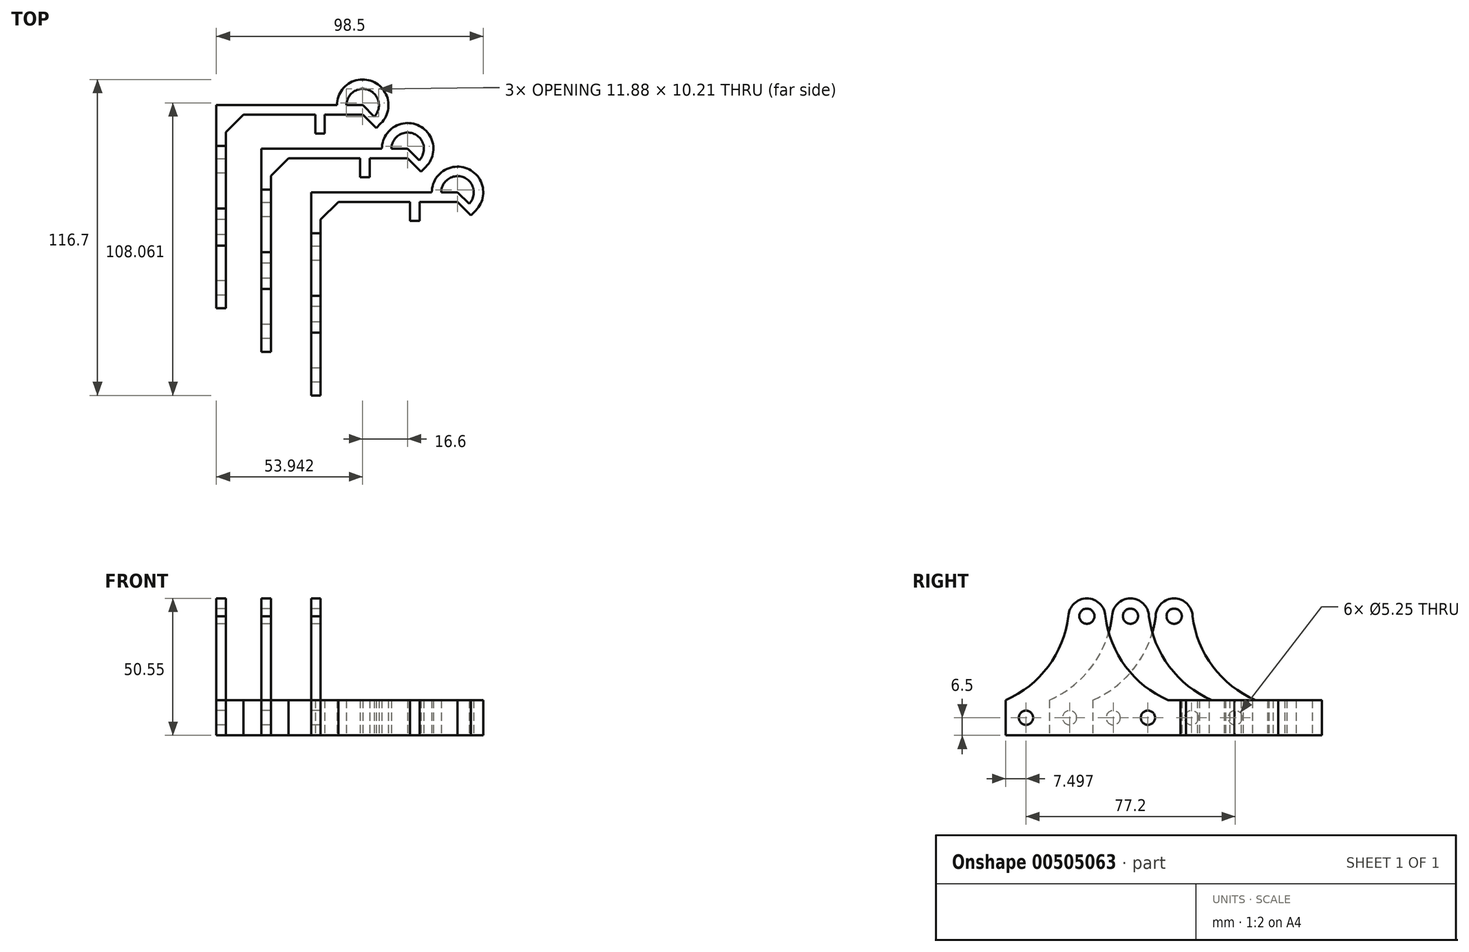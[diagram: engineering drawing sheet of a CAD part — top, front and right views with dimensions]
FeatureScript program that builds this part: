
annotation { "Feature Type Name" : "Feature", "Feature Type Description" : "" }
export const myFeature = defineFeature(function(context is Context, id is Id, definition is map)
    precondition{}
    {
        {
            var Q0;
            Q0=qCreatedBy(makeId("Top.planeOp"),FACE);
            var sketch = newSketch(context, id + "F0", { "sketchPlane" : qUnion([Q0])});
            skLineSegment(sketch, "E0", {"start": v(-36.5, -18.83) * mm, "end": v(-36.5, 56.17) * mm});
            skLineSegment(sketch, "E1", {"start": v(-36.5, 56.17) * mm, "end": v(8, 56.17) * mm});
            skLineSegment(sketch, "E2", {"start": v(17.5, 56.17) * mm, "end": v(21.74, 51.92) * mm});
            skArc(sketch, "E3", {"start": v(21.74, 51.92) * mm, "mid": v(19.8, 61.71) * mm, "end": v(11.5, 56.17) * mm});
            skArc(sketch, "E4", {"start": v(24.22, 49.45) * mm, "mid": v(21.14, 64.94) * mm, "end": v(8, 56.17) * mm});
            skLineSegment(sketch, "E5", {"start": v(-36.5, -18.83) * mm, "end": v(-33, -18.83) * mm});
            skLineSegment(sketch, "E6", {"start": v(-33, -18.83) * mm, "end": v(-33, 46.17) * mm});
            skLineSegment(sketch, "E7", {"start": v(-33, 46.17) * mm, "end": v(-26.5, 52.67) * mm});
            skLineSegment(sketch, "E8", {"start": v(-26.5, 52.67) * mm, "end": v(0, 52.67) * mm});
            skLineSegment(sketch, "E9", {"start": v(24.22, 49.45) * mm, "end": v(22.47, 47.7) * mm});
            skLineSegment(sketch, "E10", {"start": v(17.5, 52.67) * mm, "end": v(22.47, 47.7) * mm});
            skLineSegment(sketch, "E11.trimOffspring", {"start": v(11.5, 56.17) * mm, "end": v(17.5, 56.17) * mm});
            skPoint(sketch, "E12", {"position": v(-36.5, -11.83) * mm});
            skPoint(sketch, "E13", {"position": v(-36.5, 33.17) * mm});
            skPoint(sketch, "E14", {"position": v(0, 52.67) * mm});
            skLineSegment(sketch, "E15", {"start": v(0, 52.67) * mm, "end": v(0, 45.67) * mm});
            skLineSegment(sketch, "E16", {"start": v(0, 45.67) * mm, "end": v(3.5, 45.67) * mm});
            skLineSegment(sketch, "E17", {"start": v(3.5, 45.67) * mm, "end": v(3.5, 52.67) * mm});
            skLineSegment(sketch, "E18.trimOffspring", {"start": v(3.5, 52.67) * mm, "end": v(17.5, 52.67) * mm});
            skSolve(sketch);
        }
        {
            var Q0;
            Q0=makeQuery(id+"F0.imprint","IMPRINT",FACE,{"disambiguationData":[TD([[makeQuery(id+"F0.imprint","IMPRINT",EDGE,{"derivedFrom":sQuery(id+"F0.wireOp",EDGE,"E0")}),-1.0]])]});
            extrude(context, id + "F1", {"entities" : qUnion([Q0]), "depth" : 13 * mm});
        }
        {
            var Q0;
            Q0=makeQuery(id+"F1.opExtrude","SWEPT_FACE",FACE,{"disambiguationData":[OSD([sQuery(id+"F0.wireOp",EDGE,"E0")])]});
            var sketch = newSketch(context, id + "F2", { "sketchPlane" : qUnion([Q0])});
            skCircle(sketch, "E19", {"center": v(-11.14, 44) * mm, "radius": 2.81 * mm});
            skLineSegment(sketch, "E20", {"start": v(-41.12, 13) * mm, "end": v(18.83, 13) * mm});
            skPoint(sketch, "E21", {"position": v(-33.67, 6.5) * mm});
            skPoint(sketch, "E22", {"position": v(11.33, 6.5) * mm});
            skCircle(sketch, "E23", {"center": v(-33.67, 6.5) * mm, "radius": 2.62 * mm});
            skCircle(sketch, "E24", {"center": v(11.33, 6.5) * mm, "radius": 2.62 * mm});
            skPoint(sketch, "E25", {"position": v(-4.33, 44) * mm});
            skArc(sketch, "E26", {"start": v(-4.33, 44) * mm, "mid": v(3.13, 25.42) * mm, "end": v(18.83, 13) * mm});
            skArc(sketch, "E27.MirrorCS", {"start": v(-17.95, 44) * mm, "mid": v(-25.42, 25.42) * mm, "end": v(-41.12, 13) * mm});
            skArc(sketch, "E28", {"start": v(-4.33, 44) * mm, "mid": v(-11.14, 50.55) * mm, "end": v(-17.95, 44) * mm});
            skSolve(sketch);
        }
        {
            var Q0;
            Q0=makeQuery(id+"F2.imprint","IMPRINT",FACE,{"disambiguationData":[TD([[makeQuery(id+"F2.imprint","IMPRINT",EDGE,{"derivedFrom":sQuery(id+"F2.wireOp",EDGE,"E19")}),-1.0]])]});
            extrude(context, id + "F3", {"entities" : qUnion([Q0]), "operationType" : NewBodyOperationType.ADD, "oppositeDirection" : true, "depth" : 3.5 * mm});
        }
        {
            var Q0;
            Q0=makeQuery(id+"F2.imprint","IMPRINT",FACE,{"disambiguationData":[TD([[makeQuery(id+"F2.imprint","IMPRINT",EDGE,{"derivedFrom":sQuery(id+"F2.wireOp",EDGE,"E23")}),1.0]])]});
            var Q1;
            Q1=makeQuery(id+"F2.imprint","IMPRINT",FACE,{"disambiguationData":[TD([[makeQuery(id+"F2.imprint","IMPRINT",EDGE,{"derivedFrom":sQuery(id+"F2.wireOp",EDGE,"E24")}),1.0]])]});
            extrude(context, id + "F4", {"entities" : qUnion([Q0, Q1]), "operationType" : NewBodyOperationType.REMOVE, "oppositeDirection" : true, "depth" : 3.5 * mm});
        }
        {
            var Q0;
            Q0=makeQuery(id+"F1.opExtrude","SWEPT_BODY",BODY,{"disambiguationData":[OSD([sQuery(id+"F0.wireOp",EDGE,"E0"),sQuery(id+"F0.wireOp",EDGE,"E1"),sQuery(id+"F0.wireOp",EDGE,"E2"),sQuery(id+"F0.wireOp",EDGE,"E3"),sQuery(id+"F0.wireOp",EDGE,"E4"),sQuery(id+"F0.wireOp",EDGE,"E5"),sQuery(id+"F0.wireOp",EDGE,"E6"),sQuery(id+"F0.wireOp",EDGE,"E7"),sQuery(id+"F0.wireOp",EDGE,"E8"),sQuery(id+"F0.wireOp",EDGE,"E9"),sQuery(id+"F0.wireOp",EDGE,"E10"),sQuery(id+"F0.wireOp",EDGE,"E11.trimOffspring"),sQuery(id+"F0.wireOp",EDGE,"E15"),sQuery(id+"F0.wireOp",EDGE,"E16"),sQuery(id+"F0.wireOp",EDGE,"E17"),sQuery(id+"F0.wireOp",EDGE,"E18.trimOffspring")])]});
            transform(context, id + "F5", {"entities" : qUnion([Q0]), "transformType" : TransformType.TRANSLATION_3D, "dx" : 16.6 * mm, "dy" : -16.1 * mm, "dz" : 0 * mm, "makeCopy" : true});
        }
        {
            var Q0;
            Q0=makeQuery(id+"F1.opExtrude","SWEPT_BODY",BODY,{"disambiguationData":[OSD([sQuery(id+"F0.wireOp",EDGE,"E0"),sQuery(id+"F0.wireOp",EDGE,"E1"),sQuery(id+"F0.wireOp",EDGE,"E2"),sQuery(id+"F0.wireOp",EDGE,"E3"),sQuery(id+"F0.wireOp",EDGE,"E4"),sQuery(id+"F0.wireOp",EDGE,"E5"),sQuery(id+"F0.wireOp",EDGE,"E6"),sQuery(id+"F0.wireOp",EDGE,"E7"),sQuery(id+"F0.wireOp",EDGE,"E8"),sQuery(id+"F0.wireOp",EDGE,"E9"),sQuery(id+"F0.wireOp",EDGE,"E10"),sQuery(id+"F0.wireOp",EDGE,"E11.trimOffspring"),sQuery(id+"F0.wireOp",EDGE,"E15"),sQuery(id+"F0.wireOp",EDGE,"E16"),sQuery(id+"F0.wireOp",EDGE,"E17"),sQuery(id+"F0.wireOp",EDGE,"E18.trimOffspring")])]});
            transform(context, id + "F6", {"entities" : qUnion([Q0]), "transformType" : TransformType.TRANSLATION_3D, "dx" : 35 * mm, "dy" : -32.2 * mm, "dz" : 0 * mm, "makeCopy" : true});
        }
    });
